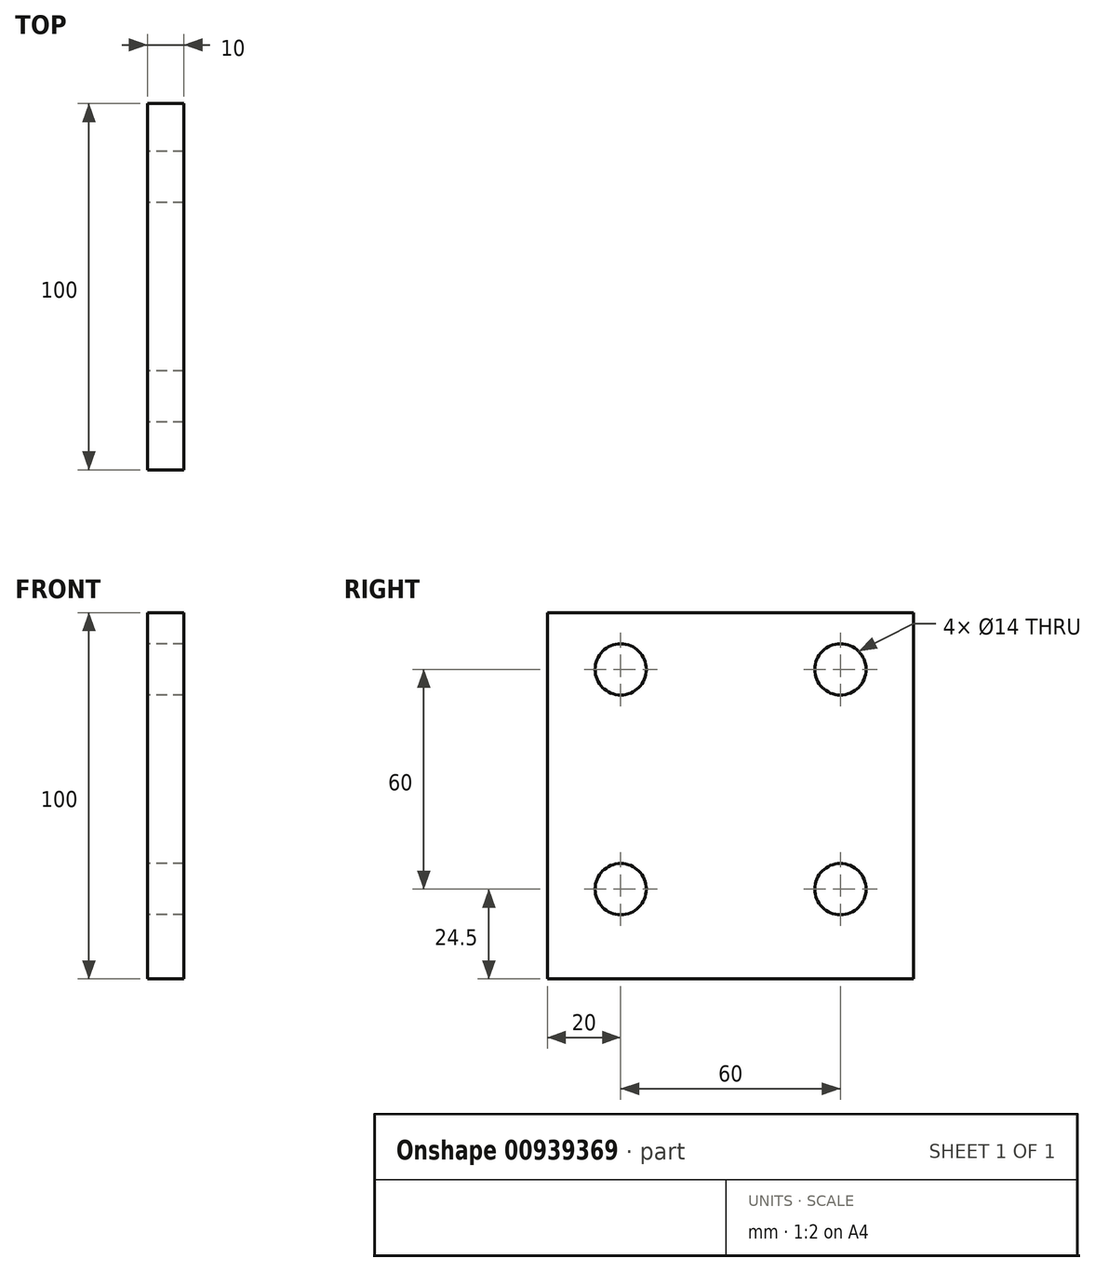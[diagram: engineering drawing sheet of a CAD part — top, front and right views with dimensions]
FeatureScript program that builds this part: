
annotation { "Feature Type Name" : "Feature", "Feature Type Description" : "" }
export const myFeature = defineFeature(function(context is Context, id is Id, definition is map)
    precondition{}
    {
        {
            var Q0;
            Q0=qCreatedBy(makeId("Right.planeOp"),FACE);
            var sketch = newSketch(context, id + "F0", { "sketchPlane" : qUnion([Q0])});
            skLineSegment(sketch, "E0.bottom", {"start": v(50, 50) * mm, "end": v(-50, 50) * mm});
            skLineSegment(sketch, "E0.top", {"start": v(50, -50) * mm, "end": v(-50, -50) * mm});
            skLineSegment(sketch, "E0.left", {"start": v(50, 50) * mm, "end": v(50, -50) * mm});
            skLineSegment(sketch, "E0.right", {"start": v(-50, 50) * mm, "end": v(-50, -50) * mm});
            skPoint(sketch, "E0.middle", {"position": v(0, 0) * mm});
            skCircle(sketch, "E1", {"center": v(-30, 34.5) * mm, "radius": 7 * mm});
            skCircle(sketch, "E2", {"center": v(-30, -25.5) * mm, "radius": 7 * mm});
            skCircle(sketch, "E3", {"center": v(30, 34.5) * mm, "radius": 7 * mm});
            skCircle(sketch, "E4", {"center": v(30, -25.5) * mm, "radius": 7 * mm});
            skSolve(sketch);
        }
        {
            var Q0;
            Q0=makeQuery(id+"F0.imprint","IMPRINT",FACE,{"disambiguationData":[TD([[makeQuery(id+"F0.imprint","IMPRINT",EDGE,{"derivedFrom":sQuery(id+"F0.wireOp",EDGE,"E0.bottom")}),1.0]])]});
            extrude(context, id + "F1", {"entities" : qUnion([Q0]), "depth" : 10 * mm, "offsetDistance" : 25 * mm});
        }
    });
